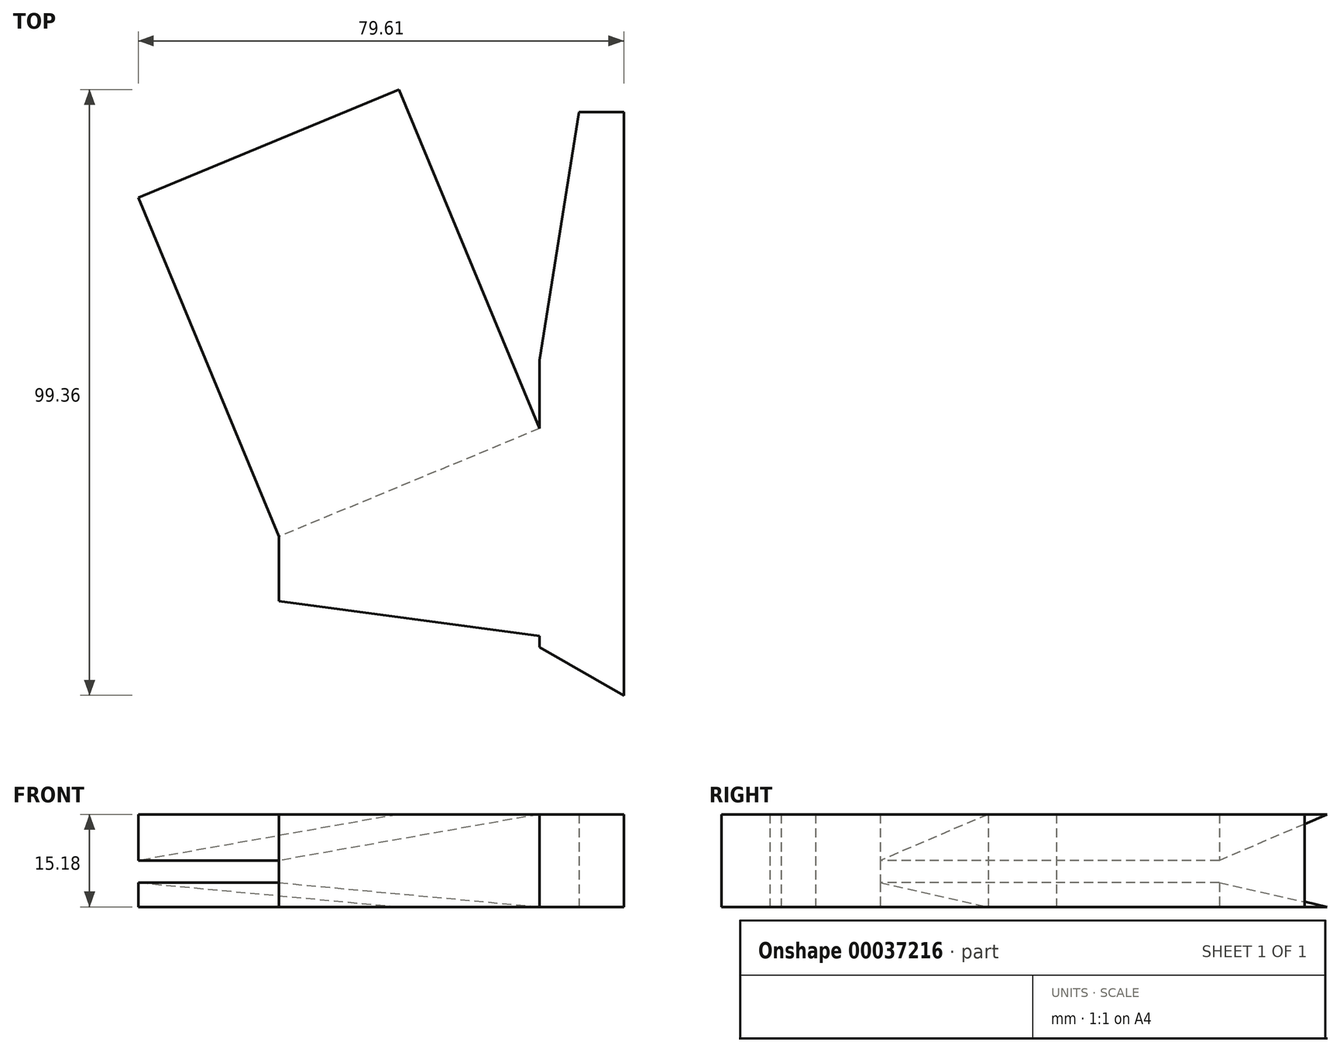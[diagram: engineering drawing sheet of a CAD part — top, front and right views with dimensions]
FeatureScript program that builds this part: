
annotation { "Feature Type Name" : "Feature", "Feature Type Description" : "" }
export const myFeature = defineFeature(function(context is Context, id is Id, definition is map)
    precondition{}
    {
        {
            var Q0;
            Q0=qCreatedBy(makeId("Top.planeOp"),FACE);
            var sketch = newSketch(context, id + "F0", { "sketchPlane" : qUnion([Q0])});
            skLineSegment(sketch, "E0", {"start": v(0, 51.9) * mm, "end": v(-7.33, 51.9) * mm});
            skLineSegment(sketch, "E1", {"start": v(-7.33, 51.9) * mm, "end": v(-13.84, 11.2) * mm});
            skLineSegment(sketch, "E2", {"start": v(-13.84, 11.2) * mm, "end": v(-13.84, -35.82) * mm});
            skLineSegment(sketch, "E3", {"start": v(-13.84, -35.82) * mm, "end": v(0, -43.75) * mm});
            skLineSegment(sketch, "E4", {"start": v(0, -43.75) * mm, "end": v(0, 51.9) * mm});
            skLineSegment(sketch, "E5", {"start": v(-13.84, 0) * mm, "end": v(-56.57, -17.7) * mm});
            skLineSegment(sketch, "E6", {"start": v(-56.57, -17.7) * mm, "end": v(-56.57, -28.29) * mm});
            skLineSegment(sketch, "E7", {"start": v(-56.57, -28.29) * mm, "end": v(0, -35.82) * mm});
            skLineSegment(sketch, "E8", {"start": v(0, -35.82) * mm, "end": v(0, 51.9) * mm});
            skLineSegment(sketch, "E9", {"start": v(-49.56, -29.22) * mm, "end": v(-49.56, -36.02) * mm});
            skLineSegment(sketch, "E10", {"start": v(-49.56, -36.02) * mm, "end": v(-42.73, -36.02) * mm});
            skLineSegment(sketch, "E11", {"start": v(-42.73, -36.02) * mm, "end": v(-42.73, -30.13) * mm});
            skLineSegment(sketch, "E12", {"start": v(-42.73, -30.13) * mm, "end": v(-49.56, -29.22) * mm});
            skLineSegment(sketch, "E13", {"start": v(-5.26, 45.65) * mm, "end": v(-8.24, 26.97) * mm});
            skFitSpline(sketch, "E14", {"points": [v(-8.24, 26.97) * mm, v(0, 22.8) * mm, v(2.95, 24) * mm, v(3.22, 24.3) * mm], "startDerivative": vector(15.94, -11.38) * mm, "endDerivative": vector(1.55, 2.15) * mm});
            skFitSpline(sketch, "E15", {"points": [v(-5.26, 45.65) * mm, v(0, 48.5) * mm, v(7.92, 47.19) * mm], "startDerivative": vector(10.56, 8.15) * mm, "endDerivative": vector(15.67, -4.75) * mm});
            skSolve(sketch);
        }
        {
            var Q0;
            {var subQ6=sQuery(id+"F0.wireOp",EDGE,"E0");Q0=makeQuery(id+"F0.imprint","IMPRINT",FACE,{"disambiguationData":[TD([[makeQuery(id+"F0.imprint","IMPRINT",EDGE,{"derivedFrom":subQ6}),1.0]])]});}
            var Q1;
            {var subQ5=sQuery(id+"F0.wireOp",EDGE,"E5");Q1=makeQuery(id+"F0.imprint","IMPRINT",FACE,{"disambiguationData":[TD([[makeQuery(id+"F0.imprint","IMPRINT",EDGE,{"derivedFrom":subQ5}),1.0]])]});}
            var Q2;
            {var subQ3=sQuery(id+"F0.wireOp",EDGE,"E13");Q2=makeQuery(id+"F0.imprint","IMPRINT",FACE,{"disambiguationData":[TD([[makeQuery(id+"F0.imprint","IMPRINT",EDGE,{"derivedFrom":subQ3}),1.0]])]});}
            var Q3;
            {var subQ4=sQuery(id+"F0.wireOp",EDGE,"E3");Q3=makeQuery(id+"F0.imprint","IMPRINT",FACE,{"disambiguationData":[TD([[makeQuery(id+"F0.imprint","IMPRINT",EDGE,{"derivedFrom":subQ4}),1.0]])]});}
            extrude(context, id + "F1", {"entities" : qUnion([Q0, Q1, Q2, Q3]), "depth" : 15.18 * mm});
        }
        {
            var Q0;
            Q0=makeQuery(id+"F1.opExtrude","SWEPT_FACE",FACE,{"disambiguationData":[OSD([sQuery(id+"F0.wireOp",EDGE,"E5")])]});
            var sketch = newSketch(context, id + "F2", { "sketchPlane" : qUnion([Q0])});
            skLineSegment(sketch, "E16", {"start": v(59.04, 3.97) * mm, "end": v(12.78, 0) * mm});
            skLineSegment(sketch, "E17", {"start": v(12.78, 0) * mm, "end": v(12.78, 15.18) * mm});
            skLineSegment(sketch, "E18", {"start": v(12.78, 15.18) * mm, "end": v(59.04, 7.59) * mm});
            skLineSegment(sketch, "E19", {"start": v(59.04, 7.59) * mm, "end": v(59.04, 3.97) * mm});
            skSolve(sketch);
        }
        {
            var Q0;
            {var subQ2=sQuery(id+"F2.wireOp",EDGE,"E18");Q0=makeQuery(id+"F2.imprint","IMPRINT",FACE,{"disambiguationData":[TD([[makeQuery(id+"F2.imprint","IMPRINT",EDGE,{"derivedFrom":subQ2}),1.0]])]});}
            var Q1;
            {var subQ2=sQuery(id+"F2.wireOp",EDGE,"E16");Q1=makeQuery(id+"F2.imprint","IMPRINT",FACE,{"disambiguationData":[TD([[makeQuery(id+"F2.imprint","IMPRINT",EDGE,{"derivedFrom":subQ2}),1.0]])]});}
            extrude(context, id + "F3", {"entities" : qUnion([Q0, Q1]), "operationType" : NewBodyOperationType.ADD, "depth" : 60.2 * mm});
        }
    });
